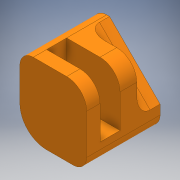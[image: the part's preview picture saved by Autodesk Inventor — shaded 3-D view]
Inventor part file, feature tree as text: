
AUTODESK INVENTOR PART (.ipt)
format: ipt  version: 2017 (Build 210142000, 142)  size: 252,928 bytes
history: native  units: mm
features: extrude x10, sketch x10, fillet x3
ambient origin geometry x8: Origin, YZ Plane, XZ Plane, XY Plane, X Axis, Y Axis, Z Axis, Center Point
bodies: Solid1 (feature_tree)
feature tree (23):
  extrude  "Extrusion1"  Depth=3.0mm
  extrude  "Extrusion2"  Depth=3.0mm
  extrude  "Extrusion3"  Depth=0.5mm TaperAngle=0.0deg
  fillet  "Fillet1"  Radius=2.0mm
  sketch  "Sketch5"  dims[d10=2.0mm d11=2.0mm]
  sketch  "Sketch7"  dims[d12=3.3333mm d15=5.8mm]
  extrude  "Extrusion8"  Depth=2.0mm
  extrude  "Extrusion10"  Depth=5.8mm
  extrude  "Extrusion11"  Depth=1.3mm TaperAngle=0.0deg
  extrude  "Extrusion12"  Depth=1.0mm TaperAngle=0.0deg
  fillet  "Fillet3"  Radius=0.25mm
  extrude  "Extrusion14"  Depth=0.3mm TaperAngle=0.0deg
  extrude  "Extrusion15"  Depth=2.0mm
  extrude  "Extrusion16"  [1 undecoded]
  fillet  "Fillet5"  [1 undecoded]
  sketch  "Sketch1"  dims[d0=5.0mm d1=3.0mm]
  sketch  "Sketch2"  dims[d2=4.0mm d3=3.0mm]
  sketch  "Sketch3"  dims[d4=5.5mm d5=0.0mm d6=0.5mm d7=0.0mm d8=2.0mm d9=0.0mm]
  sketch  "Sketch11"  dims[d25=5.5mm d26=0.0mm d30=1.3mm d31=0.0mm]
  sketch  "Sketch12"  dims[d32=1.0mm d33=0.0mm d34=1.0mm d35=0.0mm d36=0.25mm]
  sketch  "Sketch14"  dims[d41=0.3mm d42=0.0mm d43=0.2mm d44=0.0mm]
  sketch  "Sketch15"  dims[d45=0.2mm d46=0.0mm d47=2.0mm]
  sketch  "Sketch16"  dims[d48=2.0mm d49=0.0mm]
note: 2 required parameter values undecoded (feature->parameter linkage not recoverable at this tier; creation-order binding heuristic only, values carry confidence <= 0.55)
